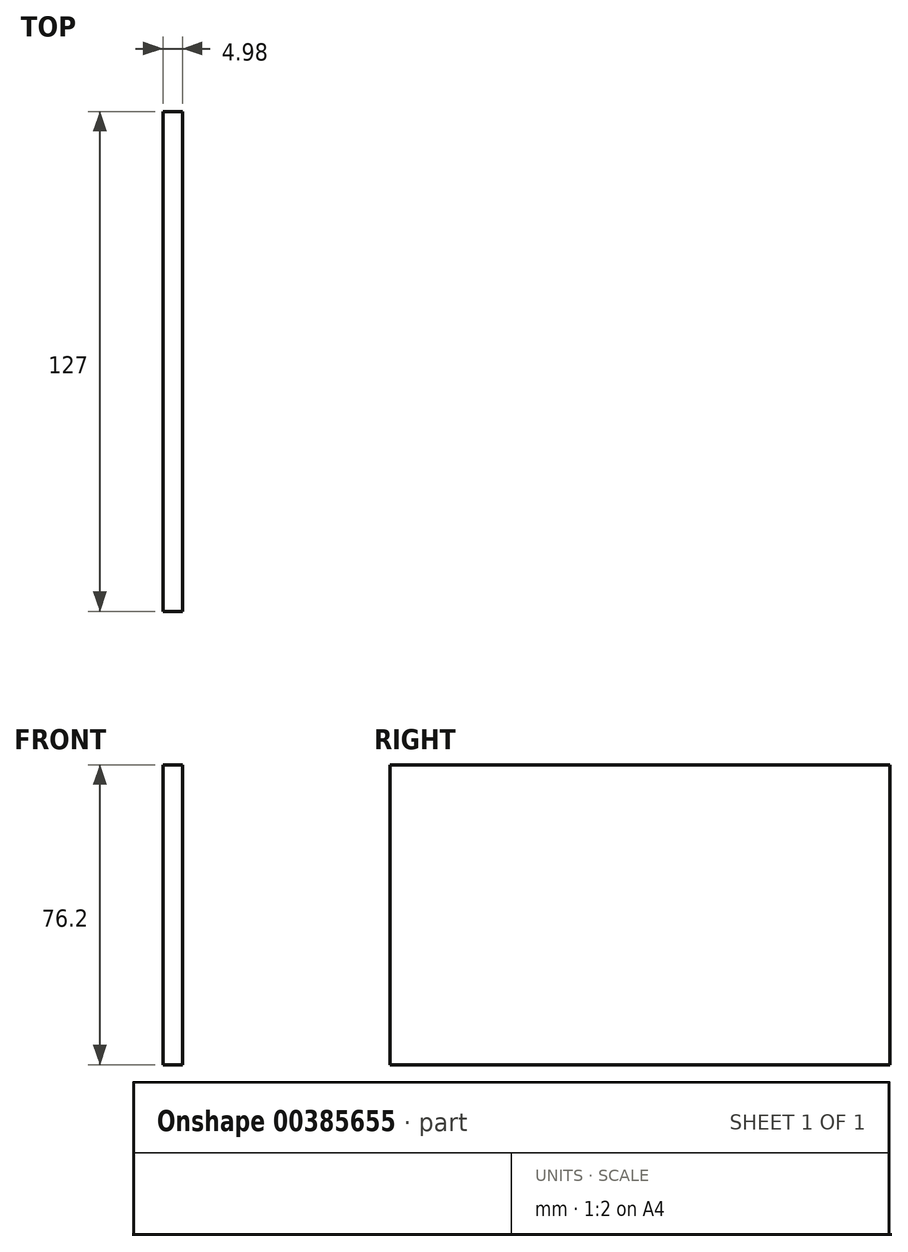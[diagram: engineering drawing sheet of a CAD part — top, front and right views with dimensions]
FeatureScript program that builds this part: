
annotation { "Feature Type Name" : "Feature", "Feature Type Description" : "" }
export const myFeature = defineFeature(function(context is Context, id is Id, definition is map)
    precondition{}
    {
        {
            var Q0;
            Q0=qCreatedBy(makeId("Right.planeOp"),FACE);
            var sketch = newSketch(context, id + "F0", { "sketchPlane" : qUnion([Q0])});
            skLineSegment(sketch, "E0.bottom", {"start": v(63.5, 38.1) * mm, "end": v(-63.5, 38.1) * mm});
            skLineSegment(sketch, "E0.top", {"start": v(63.5, -38.1) * mm, "end": v(-63.5, -38.1) * mm});
            skLineSegment(sketch, "E0.left", {"start": v(63.5, 38.1) * mm, "end": v(63.5, -38.1) * mm});
            skLineSegment(sketch, "E0.right", {"start": v(-63.5, 38.1) * mm, "end": v(-63.5, -38.1) * mm});
            skPoint(sketch, "E0.middle", {"position": v(0, 0) * mm});
            skSolve(sketch);
        }
        {
            var Q0;
            Q0=qSketchRegion(id+"F0",true);
            extrude(context, id + "F1", {"entities" : qUnion([Q0]), "depth" : 4.98 * mm});
        }
    });
